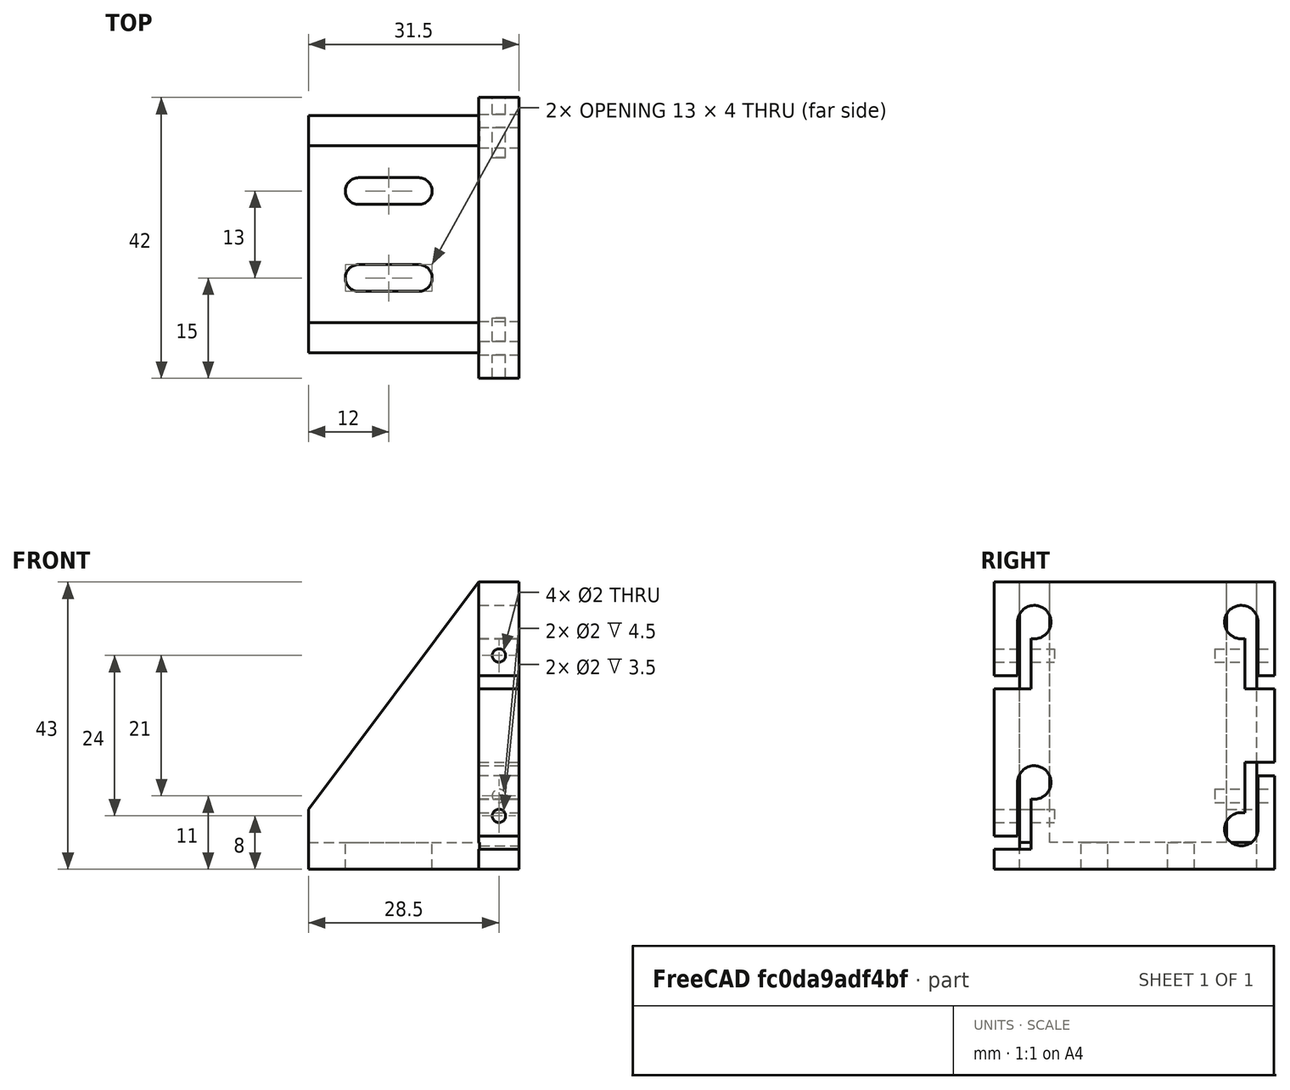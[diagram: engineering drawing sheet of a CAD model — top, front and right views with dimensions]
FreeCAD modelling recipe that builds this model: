
FCSTD DOCUMENT  (FreeCAD 0.18R16110 (Git))
Label: slider-side-wall-left
License: All rights reserved
LicenseURL: http://en.wikipedia.org/wiki/All_rights_reserved
objects: Part::Cut×18, Part::Box×11, Part::Cylinder×10, Part::MultiFuse×3, Part::Wedge×2, Mesh::Feature×1
note: 44 computed .brp shape members not serialized (recipe doc carries the construction recipe); baked Part::Feature solids carry a one-line shape summary decoded from their .brp

FEATURE [Part::Wedge] Wedge002  label="Keil002"
  AttacherType = Attacher::AttachEngine3D
  Placement = pos=(-29,7.2,-96.5) rot=(1,0,0;1.5708rad)
  X2max = 39
  X2min = 0
  Xmax = 5
  Xmin = 0
  Ymax = 25.5
  Ymin = 0
  Z2max = 4.5
  Z2min = 0
  Zmax = 4.5
  Zmin = 0
FEATURE [Part::Wedge] Wedge003  label="Keil003"
  AttacherType = Attacher::AttachEngine3D
  Placement = pos=(-29,38.2,-96.5) rot=(1,0,0;1.5708rad)
  X2max = 39
  X2min = 0
  Xmax = 5
  Xmin = 0
  Ymax = 25.5
  Ymin = 0
  Z2max = 4.5
  Z2min = 0
  Zmax = 4.5
  Zmin = 0
FEATURE [Part::Box] Box044  label="Quader038"
  AttacherType = Attacher::AttachEngine3D
  Height = 9
  Length = 10
  Placement = pos=(-31,14,27) rot=(0,0,1;0rad)
  Width = 4
FEATURE [Part::Box] Box022  label="Quader016"
  AttacherType = Attacher::AttachEngine3D
  Height = 10
  Length = 10
  Placement = pos=(-30,36.5,-73) rot=(0,0,1;0rad)
  Width = 2
FEATURE [Part::Cylinder] Cylinder130  label="Zylinder103"
  Angle = 360
  AttacherType = Attacher::AttachEngine3D
  Height = 10
  Placement = pos=(-31,16,36) rot=(0,1,0;1.5708rad)
  Radius = 2
FEATURE [Part::Box] Box023  label="Quader017"
  AttacherType = Attacher::AttachEngine3D
  Height = 10
  Length = 10
  Placement = pos=(-27,2.5,-73) rot=(0,0,1;0rad)
  Width = 2
FEATURE [Part::Box] Box018  label="Quader012"
  AttacherType = Attacher::AttachEngine3D
  Height = 10
  Length = 2
  Placement = pos=(-6,-6,-72) rot=(0,0,1;0rad)
  Width = 10
FEATURE [Part::Cylinder] Cylinder091  label="Zylinder075"
  Angle = 360
  AttacherType = Attacher::AttachEngine3D
  Height = 9
  Placement = pos=(-1,42,-68) rot=(1,0,0;1.5708rad)
  Radius = 1
FEATURE [Part::Cylinder] Cylinder092  label="Zylinder076"
  Angle = 360
  AttacherType = Attacher::AttachEngine3D
  Height = 9
  Placement = pos=(-22,9,-68) rot=(1,0,0;1.5708rad)
  Radius = 1
FEATURE [Part::Box] Box025  label="Quader019"
  AttacherType = Attacher::AttachEngine3D
  Height = 10
  Length = 2
  Placement = pos=(-19,-6,-72) rot=(0,0,1;0rad)
  Width = 10
FEATURE [Part::Box] Box040  label="Quader034"
  AttacherType = Attacher::AttachEngine3D
  Height = 25.6
  Length = 4
  Placement = pos=(-33,2.7,-96.5) rot=(0,0,1;0rad)
  Width = 35.5
FEATURE [Part::Box] Box019  label="Quader013"
  AttacherType = Attacher::AttachEngine3D
  Height = 10
  Length = 10
  Placement = pos=(-6,2.5,-73) rot=(0,0,1;0rad)
  Width = 2
FEATURE [Part::Cylinder] Cylinder129  label="Zylinder102"
  Angle = 360
  AttacherType = Attacher::AttachEngine3D
  Height = 10
  Placement = pos=(-31,16,27) rot=(0,1,0;1.5708rad)
  Radius = 2
FEATURE [Part::Box] Box020  label="Quader014"
  AttacherType = Attacher::AttachEngine3D
  Height = 10
  Length = 2
  Placement = pos=(-6,37,-72) rot=(0,0,1;0rad)
  Width = 10
FEATURE [Part::Box] Box024  label="Quader018"
  AttacherType = Attacher::AttachEngine3D
  Height = 10
  Length = 2
  Placement = pos=(-30,37,-72) rot=(0,0,1;0rad)
  Width = 10
FEATURE [Part::Box] Box021  label="Quader015"
  AttacherType = Attacher::AttachEngine3D
  Height = 10
  Length = 10
  Placement = pos=(-6,36.5,-73) rot=(0,0,1;0rad)
  Width = 2
FEATURE [Part::MultiFuse] Fusion020
  Placement = pos=(-4,-2,-116) rot=(0,0,1;0rad)
  Shapes = -> [Box044,Cylinder130,Cylinder129]
FEATURE [Part::Cut] Cut147
  Base = -> Box040
  Tool = -> Fusion020
FEATURE [Part::MultiFuse] Fusion019
  Placement = pos=(-4,11,-116) rot=(0,0,1;0rad)
  Shapes = -> [Box044,Cylinder130,Cylinder129]
FEATURE [Part::Cut] Cut148
  Base = -> Cut147
  Tool = -> Fusion019
FEATURE [Part::Cylinder] Cylinder099  label="Führung_re002"
  Angle = 360
  AttacherType = Attacher::AttachEngine3D
  Height = 6
  Placement = pos=(-27,5,-71) rot=(1,0,0;0rad)
  Radius = 2.5
FEATURE [Part::Cylinder] Cylinder090  label="Zylinder074"
  Angle = 360
  AttacherType = Attacher::AttachEngine3D
  Height = 9
  Placement = pos=(-1,9,-68) rot=(1,0,0;1.5708rad)
  Radius = 1
FEATURE [Part::Cylinder] Cylinder100  label="Führung_li003"
  Angle = 360
  AttacherType = Attacher::AttachEngine3D
  Height = 6
  Placement = pos=(4,36,-71) rot=(1,0,0;0rad)
  Radius = 2.5
FEATURE [Part::Cylinder] Cylinder101  label="Führung_re003"
  Angle = 360
  AttacherType = Attacher::AttachEngine3D
  Height = 6
  Placement = pos=(4,5,-71) rot=(1,0,0;0rad)
  Radius = 2.5
FEATURE [Part::Cylinder] Cylinder098  label="Führung_li002"
  Angle = 360
  AttacherType = Attacher::AttachEngine3D
  Height = 6
  Placement = pos=(-20,36,-71) rot=(1,0,0;0rad)
  Radius = 2.5
FEATURE [Part::Box] Box012  label="Quader007"
  AttacherType = Attacher::AttachEngine3D
  Height = 42
  Length = 43
  Placement = pos=(-33,42,-71) rot=(1,0,0;1.5708rad)
  Width = 6
FEATURE [Part::Cylinder] Cylinder093  label="Zylinder077"
  Angle = 360
  AttacherType = Attacher::AttachEngine3D
  Height = 9
  Placement = pos=(-25,42,-68) rot=(1,0,0;1.5708rad)
  Radius = 1
FEATURE [Part::Cut] Cut101
  Base = -> Box012
  Tool = -> Box018
FEATURE [Part::Cut] Cut102
  Base = -> Cut101
  Tool = -> Box019
FEATURE [Part::Cut] Cut103
  Base = -> Cut102
  Tool = -> Cylinder090
FEATURE [Part::Cut] Cut104
  Base = -> Cut103
  Tool = -> Cylinder091
FEATURE [Part::Cut] Cut105
  Base = -> Cut104
  Tool = -> Cylinder092
FEATURE [Part::Cut] Cut106
  Base = -> Cut105
  Tool = -> Cylinder093
FEATURE [Part::Cut] Cut107
  Base = -> Cut106
  Tool = -> Box020
FEATURE [Part::Cut] Cut108
  Base = -> Cut107
  Tool = -> Box021
FEATURE [Part::Cut] Cut109
  Base = -> Cut108
  Tool = -> Box022
FEATURE [Part::Cut] Cut110
  Base = -> Cut109
  Tool = -> Box023
FEATURE [Part::Cut] Cut111
  Base = -> Cut110
  Tool = -> Box024
FEATURE [Part::Cut] Cut112
  Base = -> Cut111
  Tool = -> Box025
FEATURE [Part::Cut] Cut113
  Base = -> Cut112
  Tool = -> Cylinder098
FEATURE [Part::Cut] Cut114
  Base = -> Cut113
  Tool = -> Cylinder099
FEATURE [Part::Cut] Cut115
  Base = -> Cut114
  Tool = -> Cylinder100
FEATURE [Part::Cut] Cut116  label="Wange"
  Base = -> Cut115
  Tool = -> Cylinder101
FEATURE [Part::MultiFuse] Fusion018  label="slider-side-wall-left"
  Placement = pos=(-105,140,0) rot=(0.707107,0,0.707107;3.14159rad)
  Shapes = -> [Cut148,Wedge003,Wedge002,Cut116]
FEATURE [Mesh::Feature] Mesh  label="slider-side-wall-left (Meshed)"
